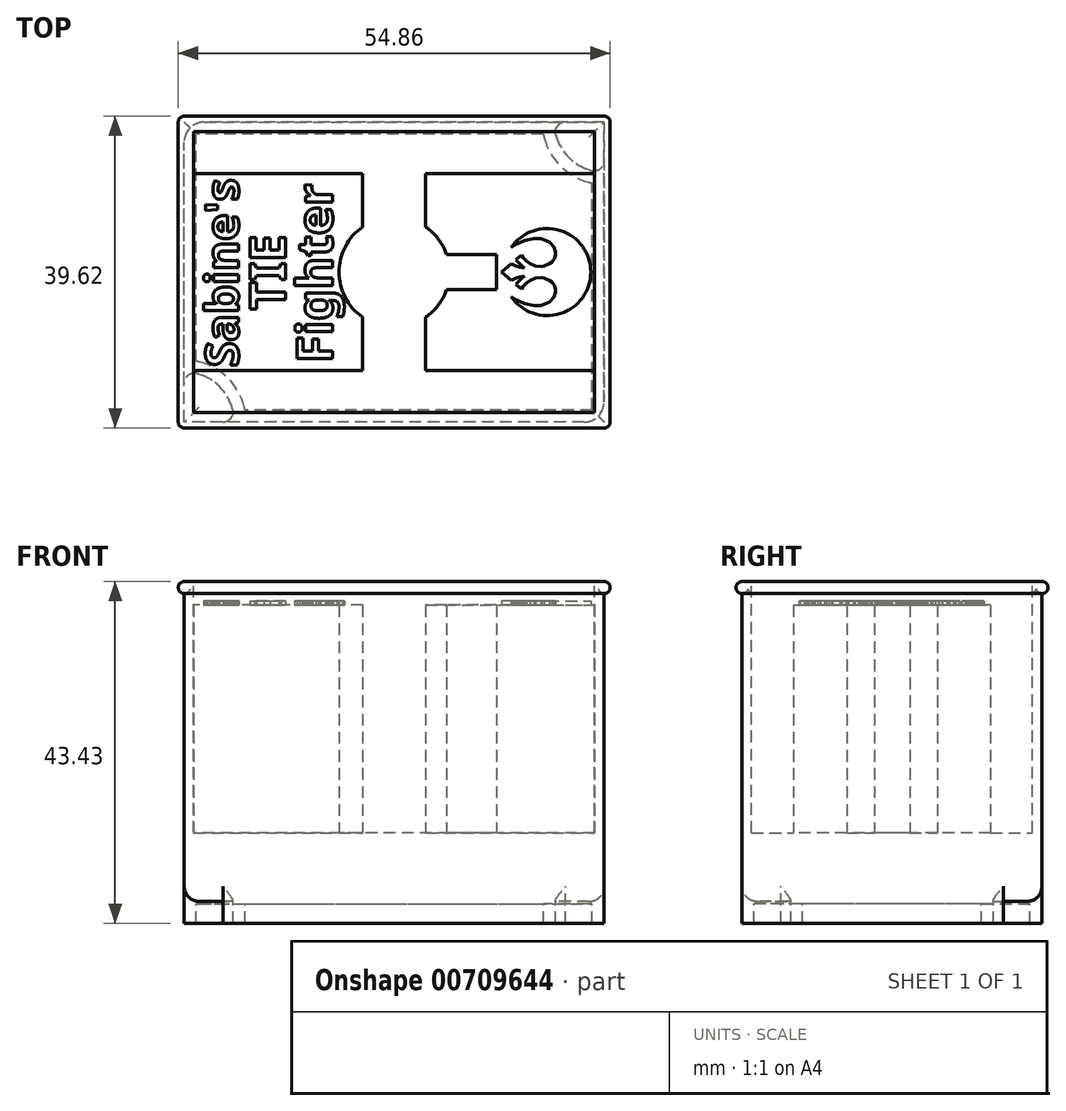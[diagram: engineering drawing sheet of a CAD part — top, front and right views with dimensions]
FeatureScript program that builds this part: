
annotation { "Feature Type Name" : "Feature", "Feature Type Description" : "" }
export const myFeature = defineFeature(function(context is Context, id is Id, definition is map)
    precondition{}
    {
        {
            var Q0;
            Q0=qCreatedBy(makeId("Front.planeOp"),FACE);
            var sketch = newSketch(context, id + "F0", { "sketchPlane" : qUnion([Q0])});
            skLineSegment(sketch, "E0.bottom", {"start": v(26.67, -20.32) * mm, "end": v(-26.67, -20.32) * mm});
            skLineSegment(sketch, "E0.top", {"start": v(26.67, 20.32) * mm, "end": v(-26.67, 20.32) * mm});
            skLineSegment(sketch, "E0.left", {"start": v(26.67, -20.32) * mm, "end": v(26.67, 20.32) * mm});
            skLineSegment(sketch, "E0.right", {"start": v(-26.67, -20.32) * mm, "end": v(-26.67, 20.32) * mm});
            skPoint(sketch, "E0.middle", {"position": v(0, 0) * mm});
            skSolve(sketch);
        }
        {
            var Q0;
            Q0=makeQuery(id+"F0.imprint","IMPRINT",FACE,{"disambiguationData":[TD([[makeQuery(id+"F0.imprint","IMPRINT",EDGE,{"derivedFrom":sQuery(id+"F0.wireOp",EDGE,"E0.bottom")}),-1.0]])]});
            extrude(context, id + "F1", {"entities" : qUnion([Q0]), "depth" : 38.1 * mm, "symmetric" : true});
        }
        {
            var Q0;
            Q0=makeQuery(id+"F1.opExtrude","SWEPT_FACE",FACE,{"disambiguationData":[OSD([sQuery(id+"F0.wireOp",EDGE,"E0.top")])]});
            shell(context, id + "F2", {"entities" : qUnion([Q0]), "thickness" : 1.2 * mm});
        }
        {
            var Q0;
            Q0=makeQuery(id+"F1.opExtrude","CAP_FACE",FACE,{"disambiguationData":[OSD([sQuery(id+"F0.wireOp",EDGE,"E0.bottom"),sQuery(id+"F0.wireOp",EDGE,"E0.top"),sQuery(id+"F0.wireOp",EDGE,"E0.left"),sQuery(id+"F0.wireOp",EDGE,"E0.right")])],"isStart":false});
            var sketch = newSketch(context, id + "F3", { "sketchPlane" : qUnion([Q0])});
            skArc(sketch, "E1", {"start": v(-26.67, 20.32) * mm, "mid": v(-27.43, 19.56) * mm, "end": v(-26.67, 18.8) * mm});
            skSolve(sketch);
        }
        {
            var Q0;
            {var subQ0=sQuery(id+"F3.wireOp",EDGE,"E1");Q0=makeQuery(id+"F3.imprint","IMPRINT",FACE,{"disambiguationData":[TD([[makeQuery(id+"F3.imprint","IMPRINT",EDGE,{"derivedFrom":subQ0}),1.0]])]});}
            var Q1;
            Q1=makeQuery(id+"F1.opExtrude","SWEPT_EDGE",EDGE,{"disambiguationData":[OSD([sQuery(id+"F0.wireOp",EDGE,"E0.top"),sQuery(id+"F0.wireOp",EDGE,"E0.right")])]});
            var Q2;
            Q2=makeQuery(id+"F1.opExtrude","CAP_EDGE",EDGE,{"disambiguationData":[OSD([sQuery(id+"F0.wireOp",EDGE,"E0.top")])],"isStart":true});
            var Q3;
            Q3=makeQuery(id+"F1.opExtrude","SWEPT_EDGE",EDGE,{"disambiguationData":[OSD([sQuery(id+"F0.wireOp",EDGE,"E0.top"),sQuery(id+"F0.wireOp",EDGE,"E0.left")])]});
            var Q4;
            Q4=makeQuery(id+"F1.opExtrude","CAP_EDGE",EDGE,{"disambiguationData":[OSD([sQuery(id+"F0.wireOp",EDGE,"E0.top")])],"isStart":false});
            sweep(context, id + "F4", {"operationType" : NewBodyOperationType.ADD, "profiles" : qUnion([Q0]), "path" : qUnion([Q1, Q2, Q3, Q4])});
        }
        {
            var Q0;
            Q0=makeQuery(id+"F1.opExtrude","SWEPT_FACE",FACE,{"disambiguationData":[OSD([sQuery(id+"F0.wireOp",EDGE,"E0.bottom")])]});
            var sketch = newSketch(context, id + "F5", { "sketchPlane" : qUnion([Q0])});
            skLineSegment(sketch, "E2.bottom", {"start": v(26.67, 19.05) * mm, "end": v(21.75, 19.05) * mm});
            skLineSegment(sketch, "E2.left", {"start": v(26.67, 19.05) * mm, "end": v(26.67, 14.13) * mm});
            skPoint(sketch, "E3.newPointA", {"position": v(20.32, 19.05) * mm});
            skArc(sketch, "E4", {"start": v(20.52, 17.46) * mm, "mid": v(22.18, 14.56) * mm, "end": v(25.08, 12.9) * mm});
            skArc(sketch, "E5.filletArc", {"start": v(21.75, 19.05) * mm, "mid": v(20.75, 18.56) * mm, "end": v(20.52, 17.46) * mm});
            skPoint(sketch, "E6.visualSharp", {"position": v(26.67, 12.7) * mm});
            skArc(sketch, "E6.filletArc", {"start": v(25.08, 12.9) * mm, "mid": v(26.18, 13.13) * mm, "end": v(26.67, 14.13) * mm});
            skArc(sketch, "E7.MirrorCS", {"start": v(-21.75, 19.05) * mm, "mid": v(-20.75, 18.56) * mm, "end": v(-20.52, 17.46) * mm});
            skArc(sketch, "E8.MirrorCS", {"start": v(-20.52, 17.46) * mm, "mid": v(-22.18, 14.56) * mm, "end": v(-25.08, 12.9) * mm});
            skArc(sketch, "E9.MirrorCS", {"start": v(-25.08, 12.9) * mm, "mid": v(-26.18, 13.13) * mm, "end": v(-26.67, 14.13) * mm});
            skLineSegment(sketch, "E10.MirrorCS", {"start": v(-26.67, 19.05) * mm, "end": v(-26.67, 14.13) * mm});
            skLineSegment(sketch, "E11.MirrorCS", {"start": v(-26.67, 19.05) * mm, "end": v(-21.75, 19.05) * mm});
            skArc(sketch, "E12.MirrorCS", {"start": v(-20.52, -17.46) * mm, "mid": v(-22.18, -14.56) * mm, "end": v(-25.08, -12.9) * mm});
            skArc(sketch, "E13.MirrorCS", {"start": v(-21.75, -19.05) * mm, "mid": v(-20.75, -18.56) * mm, "end": v(-20.52, -17.46) * mm});
            skLineSegment(sketch, "E14.MirrorCS", {"start": v(-26.67, -19.05) * mm, "end": v(-21.75, -19.05) * mm});
            skLineSegment(sketch, "E15.MirrorCS", {"start": v(-26.67, -19.05) * mm, "end": v(-26.67, -14.13) * mm});
            skArc(sketch, "E16.MirrorCS", {"start": v(-25.08, -12.9) * mm, "mid": v(-26.18, -13.13) * mm, "end": v(-26.67, -14.13) * mm});
            skArc(sketch, "E17.MirrorCS", {"start": v(21.75, -19.05) * mm, "mid": v(20.75, -18.56) * mm, "end": v(20.52, -17.46) * mm});
            skArc(sketch, "E18.MirrorCS", {"start": v(20.52, -17.46) * mm, "mid": v(22.18, -14.56) * mm, "end": v(25.08, -12.9) * mm});
            skArc(sketch, "E19.MirrorCS", {"start": v(25.08, -12.9) * mm, "mid": v(26.18, -13.13) * mm, "end": v(26.67, -14.13) * mm});
            skLineSegment(sketch, "E20.MirrorCS", {"start": v(26.67, -19.05) * mm, "end": v(26.67, -14.13) * mm});
            skLineSegment(sketch, "E21.MirrorCS", {"start": v(26.67, -19.05) * mm, "end": v(21.75, -19.05) * mm});
            skSolve(sketch);
        }
        {
            var Q0;
            Q0=makeQuery(id+"F5.imprint","IMPRINT",FACE,{"disambiguationData":[TD([[makeQuery(id+"F5.imprint","IMPRINT",EDGE,{"derivedFrom":sQuery(id+"F5.wireOp",EDGE,"E2.bottom")}),1.0]])]});
            var Q1;
            Q1=makeQuery(id+"F5.imprint","IMPRINT",FACE,{"disambiguationData":[TD([[makeQuery(id+"F5.imprint","IMPRINT",EDGE,{"derivedFrom":sQuery(id+"F5.wireOp",EDGE,"E8.MirrorCS")}),-1.0]])]});
            var Q2;
            Q2=makeQuery(id+"F5.imprint","IMPRINT",FACE,{"disambiguationData":[TD([[makeQuery(id+"F5.imprint","IMPRINT",EDGE,{"derivedFrom":sQuery(id+"F5.wireOp",EDGE,"E12.MirrorCS")}),1.0]])]});
            var Q3;
            Q3=makeQuery(id+"F5.imprint","IMPRINT",FACE,{"disambiguationData":[TD([[makeQuery(id+"F5.imprint","IMPRINT",EDGE,{"derivedFrom":sQuery(id+"F5.wireOp",EDGE,"E17.MirrorCS")}),-1.0]])]});
            extrude(context, id + "F6", {"entities" : qUnion([Q0, Q1, Q2, Q3]), "operationType" : NewBodyOperationType.ADD, "depth" : 2.8 * mm});
        }
        {
            var Q0;
            Q0=makeQuery(id+"F6.opExtrude","CAP_FACE",FACE,{"disambiguationData":[OSD([sQuery(id+"F5.wireOp",EDGE,"E2.bottom"),sQuery(id+"F5.wireOp",EDGE,"E2.left"),sQuery(id+"F5.wireOp",EDGE,"E4"),sQuery(id+"F5.wireOp",EDGE,"E5.filletArc"),sQuery(id+"F5.wireOp",EDGE,"E6.filletArc")])],"isStart":false});
            var Q1;
            Q1=makeQuery(id+"F6.opExtrude","CAP_FACE",FACE,{"disambiguationData":[OSD([sQuery(id+"F5.wireOp",EDGE,"E8.MirrorCS"),sQuery(id+"F5.wireOp",EDGE,"E9.MirrorCS"),sQuery(id+"F5.wireOp",EDGE,"E10.MirrorCS"),sQuery(id+"F5.wireOp",EDGE,"E7.MirrorCS"),sQuery(id+"F5.wireOp",EDGE,"E11.MirrorCS")])],"isStart":false});
            var Q2;
            Q2=makeQuery(id+"F6.opExtrude","CAP_FACE",FACE,{"disambiguationData":[OSD([sQuery(id+"F5.wireOp",EDGE,"E12.MirrorCS"),sQuery(id+"F5.wireOp",EDGE,"E13.MirrorCS"),sQuery(id+"F5.wireOp",EDGE,"E14.MirrorCS"),sQuery(id+"F5.wireOp",EDGE,"E15.MirrorCS"),sQuery(id+"F5.wireOp",EDGE,"E16.MirrorCS")])],"isStart":false});
            var Q3;
            Q3=makeQuery(id+"F6.opExtrude","CAP_FACE",FACE,{"disambiguationData":[OSD([sQuery(id+"F5.wireOp",EDGE,"E17.MirrorCS"),sQuery(id+"F5.wireOp",EDGE,"E18.MirrorCS"),sQuery(id+"F5.wireOp",EDGE,"E19.MirrorCS"),sQuery(id+"F5.wireOp",EDGE,"E20.MirrorCS"),sQuery(id+"F5.wireOp",EDGE,"E21.MirrorCS")])],"isStart":false});
            shell(context, id + "F7", {"entities" : qUnion([Q0, Q1, Q2, Q3]), "thickness" : 1.52 * mm});
        }
        {
            var Q0;
            Q0=makeQuery(id+"F2.opShell","OFFSET_FACE",FACE,{"disambiguationData":[OSD([sQuery(id+"F0.wireOp",EDGE,"E0.bottom")])]});
            extrude(context, id + "F8", {"entities" : qUnion([Q0]), "operationType" : NewBodyOperationType.ADD, "surfaceOperationType" : NewSurfaceOperationType.ADD, "depth" : 7.5 * mm, "offsetDistance" : 25 * mm});
        }
        {
            var Q0;
            Q0=makeQuery(id+"F1.opExtrude","SWEPT_EDGE",EDGE,{"disambiguationData":[OSD([sQuery(id+"F0.wireOp",EDGE,"E0.bottom"),sQuery(id+"F0.wireOp",EDGE,"E0.right")])]});
            var Q1;
            Q1=makeQuery(id+"F1.opExtrude","CAP_EDGE",EDGE,{"disambiguationData":[OSD([sQuery(id+"F0.wireOp",EDGE,"E0.bottom")])],"isStart":false});
            var Q2;
            Q2=makeQuery(id+"F1.opExtrude","SWEPT_EDGE",EDGE,{"disambiguationData":[OSD([sQuery(id+"F0.wireOp",EDGE,"E0.bottom"),sQuery(id+"F0.wireOp",EDGE,"E0.left")])]});
            var Q3;
            Q3=makeQuery(id+"F1.opExtrude","CAP_EDGE",EDGE,{"disambiguationData":[OSD([sQuery(id+"F0.wireOp",EDGE,"E0.bottom")])],"isStart":true});
            fillet(context, id + "F9", {"entities" : qUnion([Q0, Q1, Q2, Q3]), "radius" : 1.9 * mm, "tangentPropagation" : true, "allowEdgeOverflow" : false});
        }
        {
            var Q0;
            Q0=makeQuery(id+"F4.opSweep","MID_CAP_EDGE",EDGE,{"disambiguationData":[OSD([sQuery(id+"F0.wireOp",EDGE,"E0.top"),sQuery(id+"F0.wireOp",EDGE,"E0.left"),sQuery(id+"F3.wireOp",EDGE,"E1")])],"capPos":3.0});
            var Q1;
            Q1=makeQuery(id+"F4.opSweep","MID_CAP_EDGE",EDGE,{"disambiguationData":[OSD([sQuery(id+"F0.wireOp",EDGE,"E0.top"),sQuery(id+"F0.wireOp",EDGE,"E0.left"),sQuery(id+"F3.wireOp",EDGE,"E1")])],"capPos":2.0});
            var Q2;
            Q2=makeQuery(id+"F4.opSweep","MID_CAP_EDGE",EDGE,{"disambiguationData":[OSD([sQuery(id+"F0.wireOp",EDGE,"E0.top"),sQuery(id+"F0.wireOp",EDGE,"E0.right"),sQuery(id+"F3.wireOp",EDGE,"E1")])],"capPos":1.0});
            var Q3;
            Q3=makeQuery(id+"F4.opSweep","CAP_EDGE",EDGE,{"disambiguationData":[OSD([sQuery(id+"F0.wireOp",EDGE,"E0.top"),sQuery(id+"F0.wireOp",EDGE,"E0.right"),sQuery(id+"F3.wireOp",EDGE,"E1")])],"isStart":true});
            fillet(context, id + "F10", {"entities" : qUnion([Q0, Q1, Q2, Q3]), "radius" : 0.76 * mm, "tangentPropagation" : true, "allowEdgeOverflow" : false});
        }
        {
            var Q0;
            Q0=makeQuery(id+"F6.boolean.opBoolean","MERGE",EDGE,{"derivedFrom":[makeQuery(id+"F1.opExtrude","CAP_EDGE",EDGE,{"disambiguationData":[OSD([sQuery(id+"F0.wireOp",EDGE,"E0.left")])],"isStart":false}),makeQuery(id+"F6.opExtrude","SWEPT_EDGE",EDGE,{"disambiguationData":[OSD([sQuery(id+"F5.wireOp",EDGE,"E2.bottom"),sQuery(id+"F5.wireOp",EDGE,"E2.left")])]})]});
            var Q1;
            Q1=makeQuery(id+"F6.boolean.opBoolean","MERGE",EDGE,{"derivedFrom":[makeQuery(id+"F1.opExtrude","CAP_EDGE",EDGE,{"disambiguationData":[OSD([sQuery(id+"F0.wireOp",EDGE,"E0.left")])],"isStart":true}),makeQuery(id+"F6.opExtrude","SWEPT_EDGE",EDGE,{"disambiguationData":[OSD([sQuery(id+"F5.wireOp",EDGE,"E20.MirrorCS"),sQuery(id+"F5.wireOp",EDGE,"E21.MirrorCS")])]})]});
            var Q2;
            Q2=makeQuery(id+"F6.boolean.opBoolean","MERGE",EDGE,{"derivedFrom":[makeQuery(id+"F1.opExtrude","CAP_EDGE",EDGE,{"disambiguationData":[OSD([sQuery(id+"F0.wireOp",EDGE,"E0.right")])],"isStart":false}),makeQuery(id+"F6.opExtrude","SWEPT_EDGE",EDGE,{"disambiguationData":[OSD([sQuery(id+"F5.wireOp",EDGE,"E10.MirrorCS"),sQuery(id+"F5.wireOp",EDGE,"E11.MirrorCS")])]})]});
            var Q3;
            Q3=makeQuery(id+"F6.boolean.opBoolean","MERGE",EDGE,{"derivedFrom":[makeQuery(id+"F1.opExtrude","CAP_EDGE",EDGE,{"disambiguationData":[OSD([sQuery(id+"F0.wireOp",EDGE,"E0.right")])],"isStart":true}),makeQuery(id+"F6.opExtrude","SWEPT_EDGE",EDGE,{"disambiguationData":[OSD([sQuery(id+"F5.wireOp",EDGE,"E14.MirrorCS"),sQuery(id+"F5.wireOp",EDGE,"E15.MirrorCS")])]})]});
            fillet(context, id + "F11", {"entities" : qUnion([Q0, Q1, Q2, Q3]), "radius" : 2.54 * mm, "tangentPropagation" : true, "allowEdgeOverflow" : false});
        }
        {
            var Q0;
            Q0=makeQuery(id+"F8.opExtrude","CAP_FACE",FACE,{"disambiguationData":[OSD([sQuery(id+"F0.wireOp",EDGE,"E0.bottom")])],"isStart":false});
            var sketch = newSketch(context, id + "F12", { "sketchPlane" : qUnion([Q0])});
            skLineSegment(sketch, "E22.0", {"start": v(25.47, -17.85) * mm, "end": v(-25.47, -17.85) * mm});
            skLineSegment(sketch, "E22.1", {"start": v(-25.47, -17.85) * mm, "end": v(-25.47, 17.85) * mm});
            skLineSegment(sketch, "E22.2", {"start": v(25.47, 17.85) * mm, "end": v(-25.47, 17.85) * mm});
            skLineSegment(sketch, "E22.3", {"start": v(25.47, -17.85) * mm, "end": v(25.47, 17.85) * mm});
            skLineSegment(sketch, "E23", {"start": v(-25.15, 12.53) * mm, "end": v(-4, 12.53) * mm});
            skLineSegment(sketch, "E24", {"start": v(-25.15, -12.53) * mm, "end": v(-4, -12.53) * mm});
            skLineSegment(sketch, "E25.left", {"start": v(-4, 12.53) * mm, "end": v(-4, 5.74) * mm});
            skLineSegment(sketch, "E25.right", {"start": v(4, 12.53) * mm, "end": v(4, 5.74) * mm});
            skPoint(sketch, "E25.middle", {"position": v(0, 0) * mm});
            skArc(sketch, "E26", {"start": v(-4, 5.74) * mm, "mid": v(-7, 0) * mm, "end": v(-4, -5.74) * mm});
            skLineSegment(sketch, "E27.bottom", {"start": v(13, 2.25) * mm, "end": v(6.63, 2.25) * mm});
            skLineSegment(sketch, "E27.top", {"start": v(13, -2.25) * mm, "end": v(6.63, -2.25) * mm});
            skLineSegment(sketch, "E27.left", {"start": v(13, 2.25) * mm, "end": v(13, -2.25) * mm});
            skLineSegment(sketch, "E28.trimOffspring", {"start": v(4, -5.74) * mm, "end": v(4, -12.53) * mm});
            skLineSegment(sketch, "E29.trimOffspring", {"start": v(-4, -5.74) * mm, "end": v(-4, -12.53) * mm});
            skArc(sketch, "E30.trimOffspring", {"start": v(4, -5.74) * mm, "mid": v(5.6, -4.2) * mm, "end": v(6.63, -2.25) * mm});
            skLineSegment(sketch, "E31.trimOffspring", {"start": v(4, -12.53) * mm, "end": v(25.47, -12.53) * mm});
            skLineSegment(sketch, "E32.trimOffspring", {"start": v(4, 12.53) * mm, "end": v(25.47, 12.53) * mm});
            skArc(sketch, "E33.trimOffspring", {"start": v(6.63, 2.25) * mm, "mid": v(5.6, 4.2) * mm, "end": v(4, 5.74) * mm});
            skLineSegment(sketch, "E34", {"start": v(-25.15, -12.53) * mm, "end": v(-25.47, -12.53) * mm});
            skLineSegment(sketch, "E35", {"start": v(-25.15, 12.53) * mm, "end": v(-25.47, 12.53) * mm});
            skSolve(sketch);
        }
        {
            var Q0;
            Q0=makeQuery(id+"F12.imprint","IMPRINT",FACE,{"disambiguationData":[TD([[makeQuery(id+"F12.imprint","IMPRINT",EDGE,{"derivedFrom":sQuery(id+"F12.wireOp",EDGE,"E25.right")}),1.0]])]});
            var Q1;
            Q1=makeQuery(id+"F12.imprint","IMPRINT",FACE,{"disambiguationData":[TD([[makeQuery(id+"F12.imprint","IMPRINT",EDGE,{"derivedFrom":sQuery(id+"F12.wireOp",EDGE,"E23")}),-1.0]])]});
            var Q2;
            Q2=makeQuery(id+"F8.opExtrude","CAP_FACE",FACE,{"disambiguationData":[OSD([sQuery(id+"F0.wireOp",EDGE,"E0.bottom")])],"isStart":false});
            extrude(context, id + "F13", {"entities" : qUnion([Q0, Q1]), "operationType" : NewBodyOperationType.ADD, "depth" : 28.94 * mm, "endBoundEntityFace" : qUnion([Q2]), "offsetDistance" : 25 * mm});
        }
        {
            var Q0;
            Q0=makeQuery(id+"F13.opExtrude","CAP_FACE",FACE,{"disambiguationData":[OSD([sQuery(id+"F12.wireOp",EDGE,"E22.3"),sQuery(id+"F12.wireOp",EDGE,"E25.right"),sQuery(id+"F12.wireOp",EDGE,"E27.bottom"),sQuery(id+"F12.wireOp",EDGE,"E27.top"),sQuery(id+"F12.wireOp",EDGE,"E27.left"),sQuery(id+"F12.wireOp",EDGE,"E28.trimOffspring"),sQuery(id+"F12.wireOp",EDGE,"E30.trimOffspring"),sQuery(id+"F12.wireOp",EDGE,"E31.trimOffspring"),sQuery(id+"F12.wireOp",EDGE,"E32.trimOffspring"),sQuery(id+"F12.wireOp",EDGE,"E33.trimOffspring")])],"isStart":false});
            var sketch = newSketch(context, id + "F14", { "sketchPlane" : qUnion([Q0])});
            skCircle(sketch, "E36", {"center": v(19.45, 0) * mm, "radius": 6.35 * mm});
            skLineSegment(sketch, "E37", {"start": v(14.9, 1.1) * mm, "end": v(13.64, 0) * mm});
            skLineSegment(sketch, "E38", {"start": v(15.44, 1.6) * mm, "end": v(16.16, 2.14) * mm});
            skLineSegment(sketch, "E39", {"start": v(16.16, 2.14) * mm, "end": v(16.39, 1.84) * mm});
            skLineSegment(sketch, "E40", {"start": v(16.39, 1.84) * mm, "end": v(16.84, 1.4) * mm});
            skLineSegment(sketch, "E41", {"start": v(16.84, 1.4) * mm, "end": v(17.24, 1.08) * mm});
            skLineSegment(sketch, "E42", {"start": v(17.24, 1.08) * mm, "end": v(17.94, 0.77) * mm});
            skLineSegment(sketch, "E43", {"start": v(17.94, 0.77) * mm, "end": v(18.7, 0.7) * mm});
            skLineSegment(sketch, "E44", {"start": v(18.7, 0.7) * mm, "end": v(19.06, 0.76) * mm});
            skLineSegment(sketch, "E45", {"start": v(19.06, 0.76) * mm, "end": v(19.75, 1.07) * mm});
            skLineSegment(sketch, "E46", {"start": v(19.75, 1.07) * mm, "end": v(20.07, 1.27) * mm});
            skLineSegment(sketch, "E47", {"start": v(20.07, 1.27) * mm, "end": v(20.36, 1.7) * mm});
            skLineSegment(sketch, "E48", {"start": v(20.36, 1.7) * mm, "end": v(20.51, 2.19) * mm});
            skLineSegment(sketch, "E49", {"start": v(20.51, 2.19) * mm, "end": v(20.51, 2.56) * mm});
            skLineSegment(sketch, "E50", {"start": v(20.51, 2.56) * mm, "end": v(20.33, 3.18) * mm});
            skLineSegment(sketch, "E51", {"start": v(20.33, 3.18) * mm, "end": v(19.7, 3.83) * mm});
            skLineSegment(sketch, "E52", {"start": v(19.7, 3.83) * mm, "end": v(18.67, 4.28) * mm});
            skLineSegment(sketch, "E53", {"start": v(18.67, 4.28) * mm, "end": v(17.79, 4.28) * mm});
            skLineSegment(sketch, "E54", {"start": v(17.79, 4.28) * mm, "end": v(16.54, 3.99) * mm});
            skLineSegment(sketch, "E55", {"start": v(16.54, 3.99) * mm, "end": v(15.83, 3.69) * mm});
            skLineSegment(sketch, "E56", {"start": v(15.83, 3.69) * mm, "end": v(15.28, 3.4) * mm});
            skLineSegment(sketch, "E57", {"start": v(15.28, 3.4) * mm, "end": v(14.87, 3.1) * mm});
            skLineSegment(sketch, "E58", {"start": v(15.44, 1.6) * mm, "end": v(15.6, 1.38) * mm});
            skLineSegment(sketch, "E59", {"start": v(15.6, 1.38) * mm, "end": v(15.96, 1.02) * mm});
            skLineSegment(sketch, "E60", {"start": v(15.96, 1.02) * mm, "end": v(16.23, 0.74) * mm});
            skLineSegment(sketch, "E61", {"start": v(16.23, 0.74) * mm, "end": v(16.54, 0.53) * mm});
            skLineSegment(sketch, "E62", {"start": v(16.54, 0.53) * mm, "end": v(15.91, 0.62) * mm});
            skLineSegment(sketch, "E63", {"start": v(15.91, 0.62) * mm, "end": v(15.44, 0.78) * mm});
            skLineSegment(sketch, "E64", {"start": v(15.44, 0.78) * mm, "end": v(15.1, 0.93) * mm});
            skLineSegment(sketch, "E65", {"start": v(15.1, 0.93) * mm, "end": v(14.9, 1.1) * mm});
            skPoint(sketch, "E66.start.orphan", {"position": v(13.1, 0) * mm});
            skLineSegment(sketch, "E67.MirrorCS", {"start": v(20.07, -1.27) * mm, "end": v(20.36, -1.7) * mm});
            skLineSegment(sketch, "E68.MirrorCS", {"start": v(15.83, -3.69) * mm, "end": v(15.28, -3.4) * mm});
            skLineSegment(sketch, "E69.MirrorCS", {"start": v(19.75, -1.07) * mm, "end": v(20.07, -1.27) * mm});
            skLineSegment(sketch, "E70.MirrorCS", {"start": v(18.67, -4.28) * mm, "end": v(17.79, -4.28) * mm});
            skLineSegment(sketch, "E71.MirrorCS", {"start": v(16.54, -0.53) * mm, "end": v(15.91, -0.62) * mm});
            skLineSegment(sketch, "E72.MirrorCS", {"start": v(16.39, -1.84) * mm, "end": v(16.84, -1.4) * mm});
            skLineSegment(sketch, "E73.MirrorCS", {"start": v(15.91, -0.62) * mm, "end": v(15.44, -0.78) * mm});
            skLineSegment(sketch, "E74.MirrorCS", {"start": v(15.44, -0.78) * mm, "end": v(15.1, -0.93) * mm});
            skLineSegment(sketch, "E75.MirrorCS", {"start": v(16.23, -0.74) * mm, "end": v(16.54, -0.53) * mm});
            skLineSegment(sketch, "E76.MirrorCS", {"start": v(20.51, -2.56) * mm, "end": v(20.33, -3.18) * mm});
            skLineSegment(sketch, "E77.MirrorCS", {"start": v(20.33, -3.18) * mm, "end": v(19.7, -3.83) * mm});
            skLineSegment(sketch, "E78.MirrorCS", {"start": v(15.28, -3.4) * mm, "end": v(14.87, -3.1) * mm});
            skLineSegment(sketch, "E79.MirrorCS", {"start": v(16.54, -3.99) * mm, "end": v(15.83, -3.69) * mm});
            skLineSegment(sketch, "E80.MirrorCS", {"start": v(15.6, -1.38) * mm, "end": v(15.96, -1.02) * mm});
            skLineSegment(sketch, "E81.MirrorCS", {"start": v(16.84, -1.4) * mm, "end": v(17.24, -1.08) * mm});
            skLineSegment(sketch, "E82.MirrorCS", {"start": v(20.36, -1.7) * mm, "end": v(20.51, -2.19) * mm});
            skLineSegment(sketch, "E83.MirrorCS", {"start": v(16.16, -2.14) * mm, "end": v(16.39, -1.84) * mm});
            skLineSegment(sketch, "E84.MirrorCS", {"start": v(15.44, -1.6) * mm, "end": v(15.6, -1.38) * mm});
            skLineSegment(sketch, "E85.MirrorCS", {"start": v(19.06, -0.76) * mm, "end": v(19.75, -1.07) * mm});
            skLineSegment(sketch, "E86.MirrorCS", {"start": v(15.44, -1.6) * mm, "end": v(16.16, -2.14) * mm});
            skLineSegment(sketch, "E87.MirrorCS", {"start": v(18.7, -0.7) * mm, "end": v(19.06, -0.76) * mm});
            skLineSegment(sketch, "E88.MirrorCS", {"start": v(17.24, -1.08) * mm, "end": v(17.94, -0.77) * mm});
            skLineSegment(sketch, "E89.MirrorCS", {"start": v(17.94, -0.77) * mm, "end": v(18.7, -0.7) * mm});
            skLineSegment(sketch, "E90.MirrorCS", {"start": v(15.96, -1.02) * mm, "end": v(16.23, -0.74) * mm});
            skLineSegment(sketch, "E91.MirrorCS", {"start": v(15.1, -0.93) * mm, "end": v(14.9, -1.1) * mm});
            skLineSegment(sketch, "E92.MirrorCS", {"start": v(20.51, -2.19) * mm, "end": v(20.51, -2.56) * mm});
            skLineSegment(sketch, "E93.MirrorCS", {"start": v(17.79, -4.28) * mm, "end": v(16.54, -3.99) * mm});
            skLineSegment(sketch, "E94.MirrorCS", {"start": v(14.9, -1.1) * mm, "end": v(13.64, 0) * mm});
            skLineSegment(sketch, "E95.MirrorCS", {"start": v(19.7, -3.83) * mm, "end": v(18.67, -4.28) * mm});
            skArc(sketch, "E96", {"start": v(14.87, -3.1) * mm, "mid": v(24.98, 0) * mm, "end": v(14.87, 3.1) * mm});
            skPoint(sketch, "E97", {"position": v(19.45, 6.35) * mm});
            skPoint(sketch, "E98.0", {"position": v(12.61, 0) * mm});
            skPoint(sketch, "E99.0", {"position": v(26.28, 0) * mm});
            skLineSegment(sketch, "E100", {"start": v(13, 0) * mm, "end": v(25.47, 0) * mm, "construction": true});
            skSolve(sketch);
        }
        {
            var Q0;
            Q0=makeQuery(id+"F13.opExtrude","CAP_FACE",FACE,{"disambiguationData":[OSD([sQuery(id+"F12.wireOp",EDGE,"E22.1"),sQuery(id+"F12.wireOp",EDGE,"E23"),sQuery(id+"F12.wireOp",EDGE,"E24"),sQuery(id+"F12.wireOp",EDGE,"E25.left"),sQuery(id+"F12.wireOp",EDGE,"E26"),sQuery(id+"F12.wireOp",EDGE,"E29.trimOffspring"),sQuery(id+"F12.wireOp",EDGE,"E34"),sQuery(id+"F12.wireOp",EDGE,"E35")])],"isStart":false});
            var sketch = newSketch(context, id + "F15", { "sketchPlane" : qUnion([Q0])});
            skPoint(sketch, "E101.0", {"position": v(-22.16, -12.53) * mm});
            skPoint(sketch, "E102", {"position": v(-18.34, -11.53) * mm});
            skLineSegment(sketch, "E103", {"start": v(-13.8, 0) * mm, "end": v(-12.37, 0) * mm});
            skPoint(sketch, "E104", {"position": v(-12.37, -11.53) * mm});
            skPoint(sketch, "E105", {"position": v(-12.37, 11.53) * mm});
            skPoint(sketch, "E106", {"position": v(-13.8, 11.53) * mm});
            skPoint(sketch, "E107", {"position": v(-13.8, -11.53) * mm});
            skPoint(sketch, "E108", {"position": v(-18.34, 11.53) * mm});
            skPoint(sketch, "E109", {"position": v(-7.84, -11.53) * mm});
            skPoint(sketch, "E110", {"position": v(-7.84, 11.53) * mm});
            skText(sketch, "E111", { "text": "Fighter", "fontName": "NotoSans-Bold.ttf"});
            skPoint(sketch, "E112", {"position": v(-18.34, 0) * mm});
            skText(sketch, "E113", { "text": "TIE", "fontName": "NotoSans-Bold.ttf"});
            skPoint(sketch, "E114.0", {"position": v(-4, 12.53) * mm});
            skLineSegment(sketch, "E115.0", {"start": v(-7, 12.53) * mm, "end": v(-25.15, 12.53) * mm});
            skPoint(sketch, "E116.0", {"position": v(-4.02, 0) * mm});
            skPoint(sketch, "E117", {"position": v(-24.3, -11.53) * mm});
            skLineSegment(sketch, "E118", {"start": v(-19.78, 0) * mm, "end": v(-18.34, 0) * mm});
            skPoint(sketch, "E119", {"position": v(-24.27, 11.53) * mm});
            skPoint(sketch, "E120", {"position": v(-19.78, -11.53) * mm});
            skPoint(sketch, "E121", {"position": v(-19.78, 11.53) * mm});
            skPoint(sketch, "E122", {"position": v(-24.27, 0) * mm});
            skText(sketch, "E123", { "text": "Sabine\'s", "fontName": "NotoSans-Bold.ttf"});
            const initialGuessF15  = {"E111": [-0.00784, -0.01153, 0, 1, 0.00453], "E113": [-0.01381, -0.00482, 0, 1, 0.00452], "E123": [-0.01978, -0.01206, 0, 1, 0.0042]};
            skSetInitialGuess(sketch, initialGuessF15);
            skSolve(sketch);
        }
        {
            var Q0;
            Q0 = qSketchRegion(id + "F15", true);
            var Q1;
            Q1=makeQuery(id+"F14.imprint","IMPRINT",FACE,{"disambiguationData":[TD([[makeQuery(id+"F14.imprint","IMPRINT",EDGE,{"derivedFrom":sQuery(id+"F14.wireOp",EDGE,"E37")}),1.0]])]});
            extrude(context, id + "F16", {"entities" : qUnion([Q0, Q1]), "operationType" : NewBodyOperationType.ADD, "depth" : .5 * mm, "offsetDistance" : 25 * mm});
        }
    });
